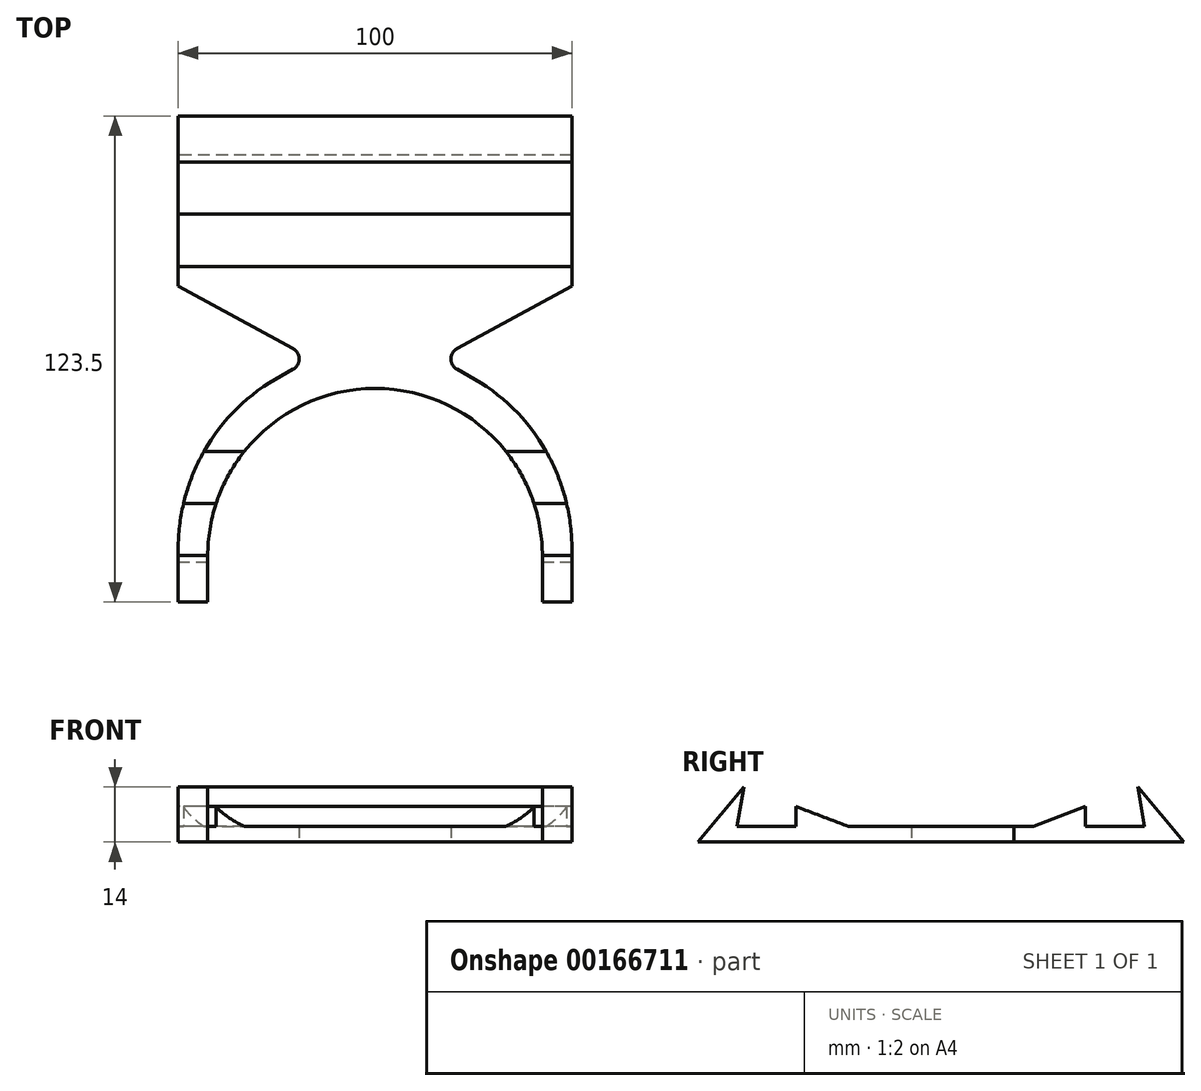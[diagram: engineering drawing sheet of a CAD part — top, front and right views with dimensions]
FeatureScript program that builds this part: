
annotation { "Feature Type Name" : "Feature", "Feature Type Description" : "" }
export const myFeature = defineFeature(function(context is Context, id is Id, definition is map)
    precondition{}
    {
        {
            var Q0;
            Q0=qCreatedBy(makeId("Right.planeOp"),FACE);
            var sketch = newSketch(context, id + "F0", { "sketchPlane" : qUnion([Q0])});
            skLineSegment(sketch, "E0", {"start": v(0, 0) * mm, "end": v(61.75, 0) * mm});
            skLineSegment(sketch, "E1", {"start": v(61.75, 0) * mm, "end": v(50, 14) * mm});
            skLineSegment(sketch, "E2", {"start": v(50, 14) * mm, "end": v(51.76, 4) * mm});
            skLineSegment(sketch, "E3", {"start": v(51.76, 4) * mm, "end": v(36.76, 4) * mm});
            skLineSegment(sketch, "E4", {"start": v(0, 4) * mm, "end": v(0, 0) * mm});
            skLineSegment(sketch, "E5", {"start": v(50, 14) * mm, "end": v(50, 0) * mm, "construction": true});
            skLineSegment(sketch, "E6", {"start": v(36.76, 4) * mm, "end": v(36.76, 9) * mm});
            skLineSegment(sketch, "E7", {"start": v(36.76, 9) * mm, "end": v(23.53, 4) * mm});
            skLineSegment(sketch, "E8.trimOffspring", {"start": v(23.53, 4) * mm, "end": v(0, 4) * mm});
            skLineSegment(sketch, "E9", {"start": v(36.76, 9) * mm, "end": v(50, 14) * mm, "construction": true});
            skSolve(sketch);
        }
        {
            var Q0;
            Q0 = qSketchRegion(id + "F0", true);
            extrude(context, id + "F1", {"entities" : qUnion([Q0]), "endBound" : BoundingType.SYMMETRIC, "depth" : 100 * mm});
        }
        {
            var Q0;
            Q0=makeQuery(id+"F1.opExtrude","SWEPT_BODY",BODY,{"disambiguationData":[OSD([sQuery(id+"F0.wireOp",EDGE,"E0"),sQuery(id+"F0.wireOp",EDGE,"E1"),sQuery(id+"F0.wireOp",EDGE,"E2"),sQuery(id+"F0.wireOp",EDGE,"E3"),sQuery(id+"F0.wireOp",EDGE,"E4"),sQuery(id+"F0.wireOp",EDGE,"E6"),sQuery(id+"F0.wireOp",EDGE,"E7"),sQuery(id+"F0.wireOp",EDGE,"E8.trimOffspring")])]});
            var Q1;
            Q1=makeQuery(id+"F1.opExtrude","SWEPT_FACE",FACE,{"disambiguationData":[OSD([sQuery(id+"F0.wireOp",EDGE,"E4")])]});
            mirror(context, id + "F2", {"operationType" : NewBodyOperationType.ADD, "entities" : qUnion([Q0]), "mirrorPlane" : qUnion([Q1])});
        }
        {
            var Q0;
            {var subQ0=makeQuery(id+"F1.opExtrude","SWEPT_FACE",FACE,{"disambiguationData":[OSD([sQuery(id+"F0.wireOp",EDGE,"E0")])]});Q0=makeQuery(id+"F2.boolean.opBoolean","MERGE",FACE,{"derivedFrom":[subQ0,makeQuery(id+"F2.opPattern","COPY",FACE,{"derivedFrom":subQ0,"instanceName":"1"})]});}
            var sketch = newSketch(context, id + "F3", { "sketchPlane" : qUnion([Q0])});
            skLineSegment(sketch, "E10", {"start": v(42.5, 61.75) * mm, "end": v(42.5, 50) * mm});
            skArc(sketch, "E11", {"start": v(0, 7.5) * mm, "mid": v(30.05, 19.95) * mm, "end": v(42.5, 50) * mm});
            skLineSegment(sketch, "E12", {"start": v(0, 7.5) * mm, "end": v(0, 61.75) * mm, "construction": true});
            skLineSegment(sketch, "E13", {"start": v(0, 61.75) * mm, "end": v(42.5, 61.75) * mm});
            skLineSegment(sketch, "E14.MirrorCS", {"start": v(-42.5, 61.75) * mm, "end": v(-42.5, 50) * mm});
            skArc(sketch, "E15.MirrorCS", {"start": v(0, 7.5) * mm, "mid": v(-30.05, 19.95) * mm, "end": v(-42.5, 50) * mm});
            skLineSegment(sketch, "E16.MirrorCS", {"start": v(0, 61.75) * mm, "end": v(-42.5, 61.75) * mm});
            skSolve(sketch);
        }
        {
            var Q0;
            Q0 = qSketchRegion(id + "F3", true);
            extrude(context, id + "F4", {"entities" : qUnion([Q0]), "operationType" : NewBodyOperationType.REMOVE, "endBound" : BoundingType.THROUGH_ALL, "oppositeDirection" : true, "depth" : 25 * mm});
        }
        {
            var Q0;
            {var subQ0=makeQuery(id+"F1.opExtrude","SWEPT_FACE",FACE,{"disambiguationData":[OSD([sQuery(id+"F0.wireOp",EDGE,"E8.trimOffspring")])]});Q0=makeQuery(id+"F2.boolean.opBoolean","MERGE",FACE,{"derivedFrom":[subQ0,makeQuery(id+"F2.opPattern","COPY",FACE,{"derivedFrom":subQ0,"instanceName":"1"})]});}
            var sketch = newSketch(context, id + "F5", { "sketchPlane" : qUnion([Q0])});
            skLineSegment(sketch, "E17", {"start": v(-50, -18.53) * mm, "end": v(-50, 18.53) * mm});
            skLineSegment(sketch, "E18", {"start": v(-50, 18.53) * mm, "end": v(-16, 0) * mm});
            skLineSegment(sketch, "E19", {"start": v(-16, 0) * mm, "end": v(-50, -18.53) * mm});
            skLineSegment(sketch, "E20.MirrorCS", {"start": v(16, 0) * mm, "end": v(50, -18.53) * mm});
            skLineSegment(sketch, "E21.MirrorCS", {"start": v(50, -18.53) * mm, "end": v(50, 18.53) * mm});
            skLineSegment(sketch, "E22.MirrorCS", {"start": v(50, 18.53) * mm, "end": v(16, 0) * mm});
            skSolve(sketch);
        }
        {
            var Q0;
            Q0 = qSketchRegion(id + "F5", true);
            var Q1;
            {var subQ0=makeQuery(id+"F1.opExtrude","SWEPT_FACE",FACE,{"disambiguationData":[OSD([sQuery(id+"F0.wireOp",EDGE,"E0")])]});Q1=makeQuery(id+"F2.boolean.opBoolean","MERGE",FACE,{"derivedFrom":[subQ0,makeQuery(id+"F2.opPattern","COPY",FACE,{"derivedFrom":subQ0,"instanceName":"1"})]});}
            extrude(context, id + "F6", {"entities" : qUnion([Q0]), "operationType" : NewBodyOperationType.REMOVE, "endBound" : BoundingType.UP_TO_SURFACE, "oppositeDirection" : true, "endBoundEntityFace" : qUnion([Q1]), "depth" : 25 * mm});
        }
        {
            var Q0;
            Q0=makeQuery(id+"F6.boolean.opBoolean","COPY",EDGE,{"derivedFrom":makeQuery(id+"F6.opExtrude","SWEPT_EDGE",EDGE,{"disambiguationData":[OSD([sQuery(id+"F0.wireOp",EDGE,"E8.trimOffspring"),sQuery(id+"F5.wireOp",EDGE,"E20.MirrorCS"),sQuery(id+"F5.wireOp",EDGE,"E21.MirrorCS")])]})});
            var Q1;
            Q1=makeQuery(id+"F6.boolean.opBoolean","COPY",EDGE,{"derivedFrom":makeQuery(id+"F6.opExtrude","SWEPT_EDGE",EDGE,{"disambiguationData":[OSD([sQuery(id+"F0.wireOp",EDGE,"E8.trimOffspring"),sQuery(id+"F5.wireOp",EDGE,"E21.MirrorCS"),sQuery(id+"F5.wireOp",EDGE,"E22.MirrorCS")])]})});
            var Q2;
            Q2=makeQuery(id+"F6.boolean.opBoolean","COPY",EDGE,{"derivedFrom":makeQuery(id+"F6.opExtrude","SWEPT_EDGE",EDGE,{"disambiguationData":[OSD([sQuery(id+"F0.wireOp",EDGE,"E8.trimOffspring"),sQuery(id+"F5.wireOp",EDGE,"E17"),sQuery(id+"F5.wireOp",EDGE,"E19")])]})});
            var Q3;
            Q3=makeQuery(id+"F6.boolean.opBoolean","COPY",EDGE,{"derivedFrom":makeQuery(id+"F6.opExtrude","SWEPT_EDGE",EDGE,{"disambiguationData":[OSD([sQuery(id+"F0.wireOp",EDGE,"E8.trimOffspring"),sQuery(id+"F5.wireOp",EDGE,"E17"),sQuery(id+"F5.wireOp",EDGE,"E18")])]})});
            fillet(context, id + "F7", {"entities" : qUnion([Q0, Q1, Q2, Q3]), "radius" : 50 * mm, "tangentPropagation" : true, "allowEdgeOverflow" : false});
        }
        {
            var Q0;
            Q0=makeQuery(id+"F6.boolean.opBoolean","COPY",EDGE,{"derivedFrom":makeQuery(id+"F6.opExtrude","SWEPT_EDGE",EDGE,{"disambiguationData":[OSD([sQuery(id+"F5.wireOp",EDGE,"E18"),sQuery(id+"F5.wireOp",EDGE,"E19")])]})});
            var Q1;
            Q1=makeQuery(id+"F6.boolean.opBoolean","COPY",EDGE,{"derivedFrom":makeQuery(id+"F6.opExtrude","SWEPT_EDGE",EDGE,{"disambiguationData":[OSD([sQuery(id+"F5.wireOp",EDGE,"E20.MirrorCS"),sQuery(id+"F5.wireOp",EDGE,"E22.MirrorCS")])]})});
            fillet(context, id + "F8", {"entities" : qUnion([Q0, Q1]), "radius" : 3 * mm, "tangentPropagation" : true, "allowEdgeOverflow" : false});
        }
    });
